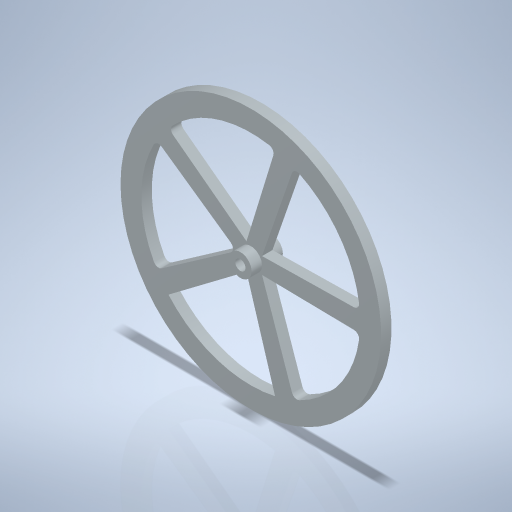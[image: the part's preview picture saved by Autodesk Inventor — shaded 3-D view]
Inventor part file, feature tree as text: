
AUTODESK INVENTOR PART (.ipt)
format: ipt  version: 2024 (Build 280153000, 153)  size: 314,368 bytes
history: native  units: mm
features: sketch x4, extrude x3, fillet x2, plane x1, hole x1, pattern_circular x1, projected_geometry x1
ambient origin geometry x8: Origin, YZ Plane, XZ Plane, XY Plane, X Axis, Y Axis, Z Axis, Center Point
bodies: Volumenkörper1 (feature_tree)
feature tree (13):
  extrude  "Extrusion1"  Depth=6.0mm TaperAngle=0.0deg
  plane  "Arbeitsebene1"
  extrude  "Extrusion3"  Depth=6.0mm TaperAngle=0.0deg
  hole  "Bohrung1"  [1 undecoded]
  extrude  "Extrusion2"  Depth=3.0mm
  fillet  "Rundung1"  Radius=50.0mm
  pattern_circular  "Runde Anordnung3"  [2 undecoded]
  fillet  "Rundung3"  Radius=6.108652mm
  sketch  "Skizze1"  dims[d0=150.0mm d1=6.0mm d2=0.0mm]
  sketch  "Skizze2"  dims[d3=126.0mm d6=6.0mm d7=0.0mm]
  projected_geometry  "Projizierte Kontur1"
  sketch  "Skizze4"  dims[d16=0.0mm d17=13.0mm]
  sketch  "Skizze5"  dims[d18=18.0mm d19=0.0mm d20=6.0mm d21=6.0mm d22=4.0mm d23=2.0mm d24=90.0deg d25=8.0mm d26=0.0mm d29=3.0mm d36=50.0mm d37=360.0deg d40=8.0mm d41=6.108652mm d42=3.0mm]
note: 3 required parameter values undecoded (feature->parameter linkage not recoverable at this tier; creation-order binding heuristic only, values carry confidence <= 0.55)
